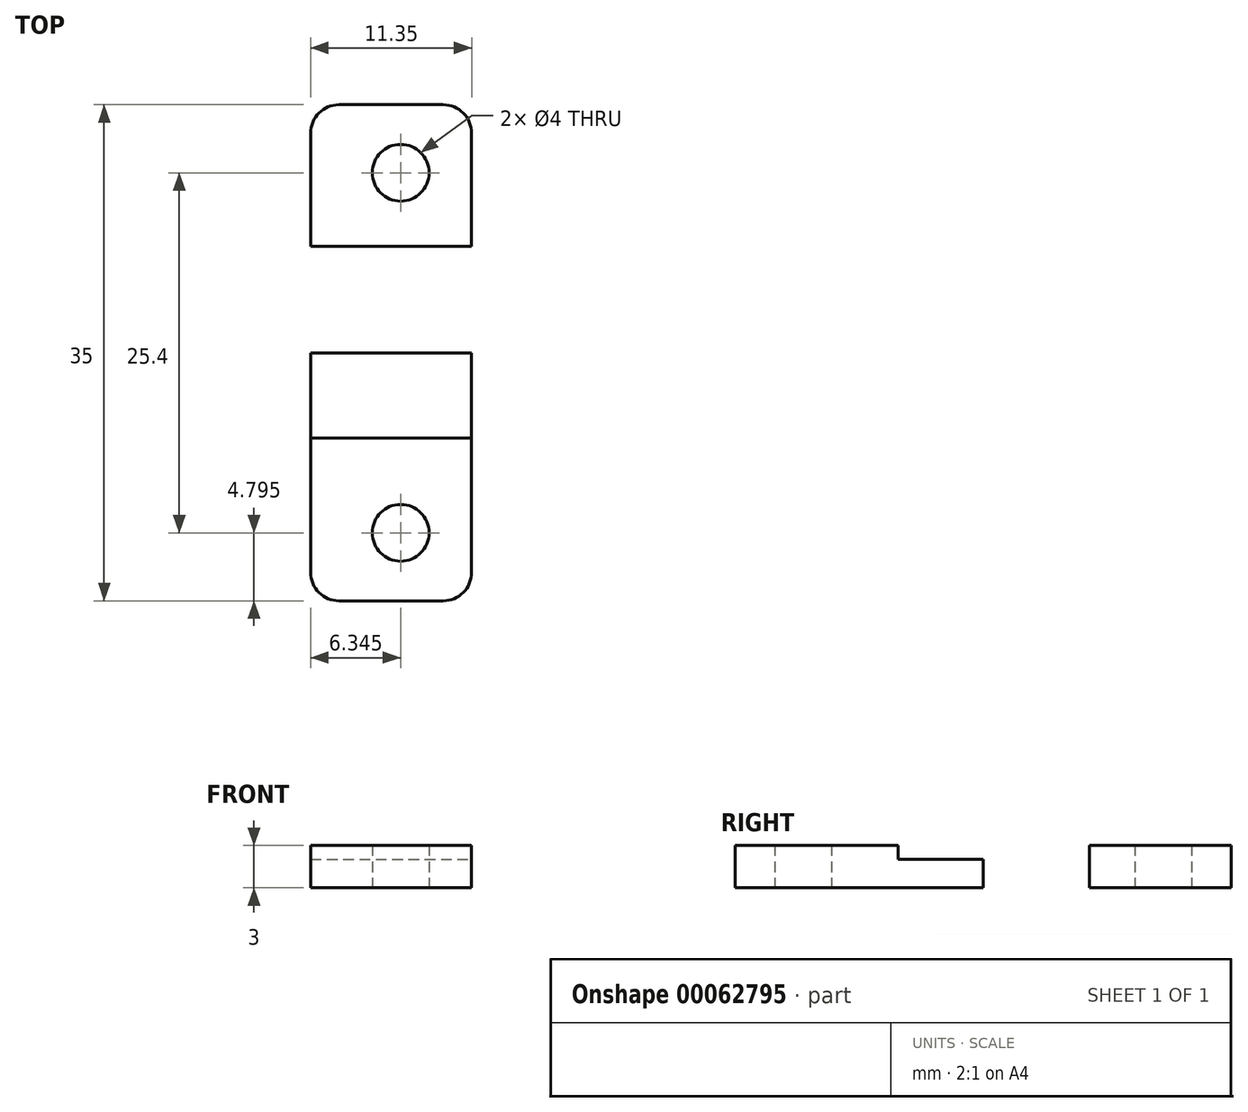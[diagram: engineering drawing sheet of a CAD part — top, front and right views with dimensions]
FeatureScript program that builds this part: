
annotation { "Feature Type Name" : "Feature", "Feature Type Description" : "" }
export const myFeature = defineFeature(function(context is Context, id is Id, definition is map)
    precondition{}
    {
        {
            var Q0;
            Q0=qCreatedBy(makeId("Top.planeOp"),FACE);
            var sketch = newSketch(context, id + "F0", { "sketchPlane" : qUnion([Q0])});
            skPoint(sketch, "E0", {"position": v(0.28, -0.97) * mm});
            skLineSegment(sketch, "E1", {"start": v(-6.07, -6.17) * mm, "end": v(11.93, -6.17) * mm, "construction": true});
            skLineSegment(sketch, "E2.bottom", {"start": v(5.28, -6.17) * mm, "end": v(-6.07, -6.17) * mm});
            skLineSegment(sketch, "E2.top", {"start": v(3.28, 3.83) * mm, "end": v(-4.07, 3.83) * mm});
            skLineSegment(sketch, "E2.left", {"start": v(5.28, -6.17) * mm, "end": v(5.27, 1.83) * mm});
            skLineSegment(sketch, "E2.right", {"start": v(-6.07, -6.17) * mm, "end": v(-6.07, 1.83) * mm});
            skPoint(sketch, "E3.visualSharp", {"position": v(-6.07, 3.83) * mm});
            skArc(sketch, "E3.filletArc", {"start": v(-4.07, 3.83) * mm, "mid": v(-5.49, 3.24) * mm, "end": v(-6.07, 1.83) * mm});
            skPoint(sketch, "E4.visualSharp", {"position": v(5.27, 3.83) * mm});
            skArc(sketch, "E4.filletArc", {"start": v(5.28, 1.83) * mm, "mid": v(4.69, 3.24) * mm, "end": v(3.28, 3.83) * mm});
            skCircle(sketch, "E5", {"center": v(0.28, -0.97) * mm, "radius": 2 * mm});
            skLineSegment(sketch, "E6.bottom", {"start": v(-6.07, -6.17) * mm, "end": v(5.28, -6.17) * mm});
            skLineSegment(sketch, "E6.top", {"start": v(-6.07, -13.67) * mm, "end": v(5.28, -13.67) * mm});
            skLineSegment(sketch, "E6.left", {"start": v(-6.07, -6.17) * mm, "end": v(-6.07, -13.67) * mm});
            skLineSegment(sketch, "E6.right", {"start": v(5.28, -6.17) * mm, "end": v(5.28, -13.67) * mm});
            skLineSegment(sketch, "E7.MirrorCS", {"start": v(-6.07, -21.17) * mm, "end": v(-6.07, -13.67) * mm});
            skLineSegment(sketch, "E8.MirrorCS", {"start": v(-6.07, -21.17) * mm, "end": v(-6.07, -29.17) * mm});
            skArc(sketch, "E9.MirrorCS", {"start": v(-4.07, -31.17) * mm, "mid": v(-5.49, -30.59) * mm, "end": v(-6.07, -29.17) * mm});
            skLineSegment(sketch, "E10.MirrorCS", {"start": v(3.28, -31.17) * mm, "end": v(-4.07, -31.17) * mm});
            skArc(sketch, "E11.MirrorCS", {"start": v(5.28, -29.17) * mm, "mid": v(4.69, -30.59) * mm, "end": v(3.28, -31.17) * mm});
            skLineSegment(sketch, "E12.MirrorCS", {"start": v(5.28, -21.17) * mm, "end": v(5.27, -29.17) * mm});
            skLineSegment(sketch, "E13.MirrorCS", {"start": v(5.28, -21.17) * mm, "end": v(5.28, -13.67) * mm});
            skCircle(sketch, "E14.MirrorC", {"center": v(0.28, -26.37) * mm, "radius": 2 * mm});
            skSolve(sketch);
        }
        {
            var Q0;
            Q0=makeQuery(id+"F0.imprint","IMPRINT",FACE,{"disambiguationData":[TD([[makeQuery(id+"F0.imprint","IMPRINT",EDGE,{"derivedFrom":sQuery(id+"F0.wireOp",EDGE,"E2.bottom")}),-1.0]])]});
            var Q1;
            Q1=makeQuery(id+"F0.imprint","IMPRINT",FACE,{"disambiguationData":[TD([[makeQuery(id+"F0.imprint","IMPRINT",EDGE,{"derivedFrom":sQuery(id+"F0.wireOp",EDGE,"E6.top")}),-1.0]])]});
            var Q2;
            Q2=makeQuery(id+"F0.imprint","IMPRINT",FACE,{"disambiguationData":[TD([[makeQuery(id+"F0.imprint","IMPRINT",EDGE,{"derivedFrom":sQuery(id+"F0.wireOp",EDGE,"E6.bottom")}),-1.0]])]});
            var Q3;
            Q3=makeQuery(id+"F0.imprint","IMPRINT",FACE,{"disambiguationData":[TD([[makeQuery(id+"F0.imprint","IMPRINT",EDGE,{"derivedFrom":sQuery(id+"F0.wireOp",EDGE,"E2.top")}),1.0]])]});
            extrude(context, id + "F1", {"entities" : qUnion([Q0, Q1, Q2, Q3]), "depth" : 3 * mm});
        }
        {
            var Q0;
            Q0=makeQuery(id+"F1.opExtrude","CAP_FACE",FACE,{"disambiguationData":[OSD([sQuery(id+"F0.wireOp",EDGE,"E2.top"),sQuery(id+"F0.wireOp",EDGE,"E2.left"),sQuery(id+"F0.wireOp",EDGE,"E2.right"),sQuery(id+"F0.wireOp",EDGE,"E3.filletArc"),sQuery(id+"F0.wireOp",EDGE,"E4.filletArc"),sQuery(id+"F0.wireOp",EDGE,"E5"),sQuery(id+"F0.wireOp",EDGE,"E6.left"),sQuery(id+"F0.wireOp",EDGE,"E6.right"),sQuery(id+"F0.wireOp",EDGE,"E7.MirrorCS"),sQuery(id+"F0.wireOp",EDGE,"E8.MirrorCS"),sQuery(id+"F0.wireOp",EDGE,"E9.MirrorCS"),sQuery(id+"F0.wireOp",EDGE,"E10.MirrorCS"),sQuery(id+"F0.wireOp",EDGE,"E11.MirrorCS"),sQuery(id+"F0.wireOp",EDGE,"E12.MirrorCS"),sQuery(id+"F0.wireOp",EDGE,"E13.MirrorCS"),sQuery(id+"F0.wireOp",EDGE,"E14.MirrorC")])],"isStart":false});
            var sketch = newSketch(context, id + "F2", { "sketchPlane" : qUnion([Q0])});
            skLineSegment(sketch, "E15.bottom", {"start": v(-6.07, -19.67) * mm, "end": v(5.28, -19.67) * mm});
            skLineSegment(sketch, "E15.top", {"start": v(-6.07, -7.67) * mm, "end": v(5.28, -7.67) * mm});
            skLineSegment(sketch, "E15.left", {"start": v(-6.07, -19.67) * mm, "end": v(-6.07, -7.67) * mm});
            skLineSegment(sketch, "E15.right", {"start": v(5.28, -19.67) * mm, "end": v(5.28, -7.67) * mm});
            skSolve(sketch);
        }
        {
            var Q0;
            Q0=makeQuery(id+"F2.imprint","IMPRINT",FACE,{"disambiguationData":[TD([[makeQuery(id+"F2.imprint","IMPRINT",EDGE,{"derivedFrom":sQuery(id+"F2.wireOp",EDGE,"E15.bottom")}),1.0]])]});
            extrude(context, id + "F3", {"entities" : qUnion([Q0]), "operationType" : NewBodyOperationType.REMOVE, "oppositeDirection" : true, "depth" : 1 * mm});
        }
    });
